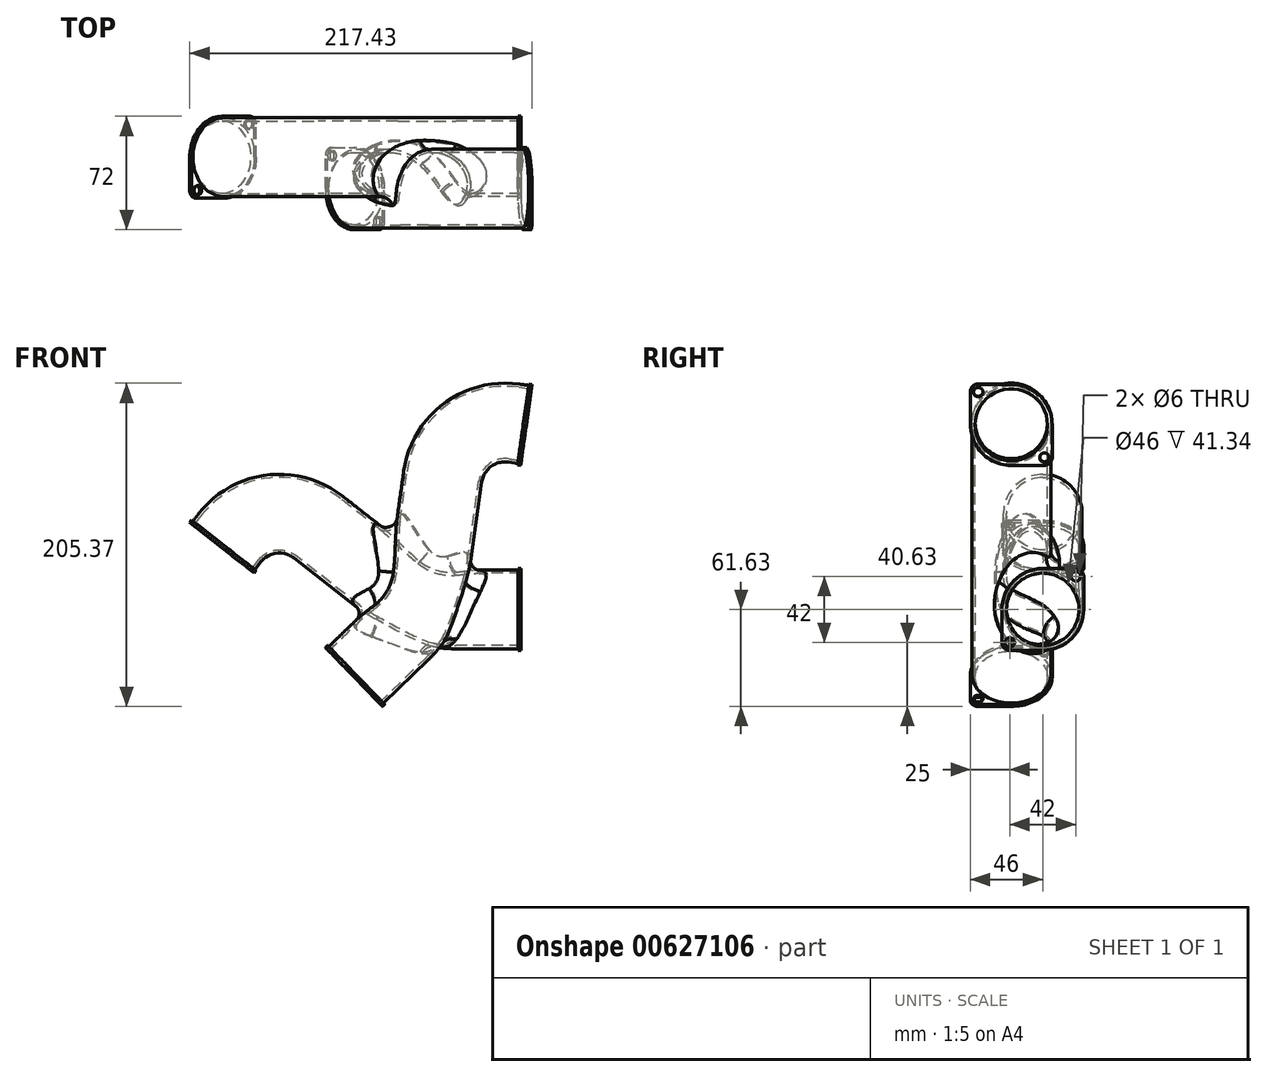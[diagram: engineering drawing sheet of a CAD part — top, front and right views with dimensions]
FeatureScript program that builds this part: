
annotation { "Feature Type Name" : "Feature", "Feature Type Description" : "" }
export const myFeature = defineFeature(function(context is Context, id is Id, definition is map)
    precondition{}
    {
        {
            var Q0;
            Q0=qCreatedBy(makeId("Right.planeOp"),FACE);
            var sketch = newSketch(context, id + "F0", { "sketchPlane" : qUnion([Q0])});
            skLineSegment(sketch, "E0.bottom", {"start": v(0, 26) * mm, "end": v(21, 26) * mm});
            skLineSegment(sketch, "E0.top", {"start": v(-21, -26) * mm, "end": v(0, -26) * mm});
            skLineSegment(sketch, "E0.left", {"start": v(-26, 0) * mm, "end": v(-26, -21) * mm});
            skLineSegment(sketch, "E0.right", {"start": v(26, 21) * mm, "end": v(26, 0) * mm});
            skPoint(sketch, "E0.middle", {"position": v(0, 0) * mm});
            skPoint(sketch, "E1.visualSharp", {"position": v(-26, 26) * mm});
            skArc(sketch, "E1.filletArc", {"start": v(0, 26) * mm, "mid": v(-18.38, 18.38) * mm, "end": v(-26, 0) * mm});
            skPoint(sketch, "E2.visualSharp", {"position": v(26, -26) * mm});
            skArc(sketch, "E2.filletArc", {"start": v(0, -26) * mm, "mid": v(18.38, -18.38) * mm, "end": v(26, 0) * mm});
            skPoint(sketch, "E3.visualSharp", {"position": v(-26, -26) * mm});
            skArc(sketch, "E3.filletArc", {"start": v(-26, -21) * mm, "mid": v(-24.54, -24.54) * mm, "end": v(-21, -26) * mm});
            skPoint(sketch, "E4.visualSharp", {"position": v(26, 26) * mm});
            skArc(sketch, "E4.filletArc", {"start": v(26, 21) * mm, "mid": v(24.54, 24.54) * mm, "end": v(21, 26) * mm});
            skCircle(sketch, "E5", {"center": v(21, 21) * mm, "radius": 3 * mm});
            skCircle(sketch, "E6", {"center": v(-21, -21) * mm, "radius": 3 * mm});
            skSolve(sketch);
        }
        {
            var Q0;
            Q0 = qSketchRegion(id + "F0", true);
            extrude(context, id + "F1", {"entities" : qUnion([Q0]), "depth" : 2 * mm, "offsetDistance" : 25 * mm});
        }
        {
            var Q0;
            Q0=makeQuery(id+"F1.opExtrude","CAP_FACE",FACE,{"disambiguationData":[OSD([sQuery(id+"F0.wireOp",EDGE,"E0.bottom"),sQuery(id+"F0.wireOp",EDGE,"E0.top"),sQuery(id+"F0.wireOp",EDGE,"E0.left"),sQuery(id+"F0.wireOp",EDGE,"E0.right"),sQuery(id+"F0.wireOp",EDGE,"E1.filletArc"),sQuery(id+"F0.wireOp",EDGE,"E2.filletArc"),sQuery(id+"F0.wireOp",EDGE,"E3.filletArc"),sQuery(id+"F0.wireOp",EDGE,"E4.filletArc"),sQuery(id+"F0.wireOp",EDGE,"E5"),sQuery(id+"F0.wireOp",EDGE,"E6")])],"isStart":true});
            var sketch = newSketch(context, id + "F2", { "sketchPlane" : qUnion([Q0])});
            skCircle(sketch, "E7", {"center": v(0, 0) * mm, "radius": 25 * mm});
            skSolve(sketch);
        }
        {
            var Q0;
            Q0=qCreatedBy(makeId("Front.planeOp"),FACE);
            var sketch = newSketch(context, id + "F3", { "sketchPlane" : qUnion([Q0])});
            skLineSegment(sketch, "E8", {"start": v(0, 0) * mm, "end": v(-39.34, 0) * mm});
            skLineSegment(sketch, "E9", {"start": v(-76.28, 12.72) * mm, "end": v(-126.98, 52.33) * mm});
            skLineSegment(sketch, "E10", {"start": v(-183.13, 45.44) * mm, "end": v(-186.82, 40.7) * mm});
            skPoint(sketch, "E11.visualSharp", {"position": v(-60, 0) * mm});
            skArc(sketch, "E11.filletArc", {"start": v(-76.28, 12.72) * mm, "mid": v(-58.87, 3.27) * mm, "end": v(-39.34, 0) * mm});
            skPoint(sketch, "E12.visualSharp", {"position": v(-158.5, 76.96) * mm});
            skArc(sketch, "E12.filletArc", {"start": v(-126.98, 52.33) * mm, "mid": v(-156.48, 60.51) * mm, "end": v(-183.13, 45.44) * mm});
            skSolve(sketch);
        }
        {
            var Q0;
            Q0=makeQuery(id+"F2.imprint","IMPRINT",FACE,{"disambiguationData":[TD([[makeQuery(id+"F2.imprint","IMPRINT",EDGE,{"derivedFrom":sQuery(id+"F2.wireOp",EDGE,"E7")}),1.0]])]});
            var Q1;
            Q1=sQuery(id+"F3.wireOp",EDGE,"E8");
            var Q2;
            Q2=sQuery(id+"F3.wireOp",EDGE,"E11.filletArc");
            var Q3;
            Q3=sQuery(id+"F3.wireOp",EDGE,"E9");
            var Q4;
            Q4=sQuery(id+"F3.wireOp",EDGE,"E12.filletArc");
            var Q5;
            Q5=sQuery(id+"F3.wireOp",EDGE,"E10");
            sweep(context, id + "F4", {"operationType" : NewBodyOperationType.ADD, "profiles" : qUnion([Q0]), "path" : qUnion([Q1, Q2, Q3, Q4, Q5])});
        }
        {
            var Q0;
            Q0=makeQuery(id+"F4.opSweep","CAP_FACE",FACE,{"disambiguationData":[OSD([sQuery(id+"F2.wireOp",EDGE,"E7"),sQuery(id+"F3.wireOp",VERTEX,"E10.end")])],"isStart":false});
            var sketch = newSketch(context, id + "F5", { "sketchPlane" : qUnion([Q0])});
            skLineSegment(sketch, "E13.bottom", {"start": v(-193.28, 26) * mm, "end": v(-172.28, 26) * mm});
            skLineSegment(sketch, "E13.top", {"start": v(-172.28, -26) * mm, "end": v(-151.28, -26) * mm});
            skLineSegment(sketch, "E13.left", {"start": v(-198.28, 21) * mm, "end": v(-198.28, 0) * mm});
            skLineSegment(sketch, "E13.right", {"start": v(-146.28, 0) * mm, "end": v(-146.28, -21) * mm});
            skPoint(sketch, "E13.middle", {"position": v(-172.28, 0) * mm});
            skPoint(sketch, "E14.visualSharp", {"position": v(-198.28, -26) * mm});
            skArc(sketch, "E14.filletArc", {"start": v(-198.28, 0) * mm, "mid": v(-190.67, -18.38) * mm, "end": v(-172.28, -26) * mm});
            skPoint(sketch, "E15.visualSharp", {"position": v(-146.28, 26) * mm});
            skArc(sketch, "E15.filletArc", {"start": v(-146.28, 0) * mm, "mid": v(-153.9, 18.38) * mm, "end": v(-172.28, 26) * mm});
            skPoint(sketch, "E16.visualSharp", {"position": v(-146.28, -26) * mm});
            skArc(sketch, "E16.filletArc", {"start": v(-151.28, -26) * mm, "mid": v(-147.75, -24.54) * mm, "end": v(-146.28, -21) * mm});
            skPoint(sketch, "E17.visualSharp", {"position": v(-198.28, 26) * mm});
            skArc(sketch, "E17.filletArc", {"start": v(-193.28, 26) * mm, "mid": v(-196.82, 24.54) * mm, "end": v(-198.28, 21) * mm});
            skCircle(sketch, "E18", {"center": v(-193.28, 21) * mm, "radius": 3 * mm});
            skCircle(sketch, "E19", {"center": v(-151.28, -21) * mm, "radius": 3 * mm});
            skSolve(sketch);
        }
        {
            var Q0;
            Q0 = qSketchRegion(id + "F5", true);
            extrude(context, id + "F6", {"entities" : qUnion([Q0]), "operationType" : NewBodyOperationType.ADD, "depth" : 2 * mm, "offsetDistance" : 25 * mm});
        }
        {
            var Q0;
            Q0=qCreatedBy(makeId("Top.planeOp"),FACE);
            var sketch = newSketch(context, id + "F7", { "sketchPlane" : qUnion([Q0])});
            skLineSegment(sketch, "E20", {"start": v(-59.8, 45.05) * mm, "end": v(-59.8, -43.57) * mm, "construction": true});
            skSolve(sketch);
        }
        {
            var Q0;
            Q0=sQuery(id+"F7.wireOp",EDGE,"E20");
            var Q1;
            Q1=makeQuery(id+"F1.opExtrude","CAP_FACE",FACE,{"disambiguationData":[OSD([sQuery(id+"F0.wireOp",EDGE,"E0.bottom"),sQuery(id+"F0.wireOp",EDGE,"E0.top"),sQuery(id+"F0.wireOp",EDGE,"E0.left"),sQuery(id+"F0.wireOp",EDGE,"E0.right"),sQuery(id+"F0.wireOp",EDGE,"E1.filletArc"),sQuery(id+"F0.wireOp",EDGE,"E2.filletArc"),sQuery(id+"F0.wireOp",EDGE,"E3.filletArc"),sQuery(id+"F0.wireOp",EDGE,"E4.filletArc"),sQuery(id+"F0.wireOp",EDGE,"E5"),sQuery(id+"F0.wireOp",EDGE,"E6")])],"isStart":false});
            cPlane(context, id + "F8", {"entities" : qUnion([Q0, Q1]), "cplaneType" : CPlaneType.LINE_ANGLE, "offset" : 25 * mm, "angle" : 22 * degree, "width" : 150 * mm, "height" : 150 * mm});
        }
        {
            var Q0;
            Q0=makeQuery(id+"F1.opExtrude","SWEPT_BODY",BODY,{"disambiguationData":[OSD([sQuery(id+"F0.wireOp",EDGE,"E0.bottom"),sQuery(id+"F0.wireOp",EDGE,"E0.top"),sQuery(id+"F0.wireOp",EDGE,"E0.left"),sQuery(id+"F0.wireOp",EDGE,"E0.right"),sQuery(id+"F0.wireOp",EDGE,"E1.filletArc"),sQuery(id+"F0.wireOp",EDGE,"E2.filletArc"),sQuery(id+"F0.wireOp",EDGE,"E3.filletArc"),sQuery(id+"F0.wireOp",EDGE,"E4.filletArc"),sQuery(id+"F0.wireOp",EDGE,"E5"),sQuery(id+"F0.wireOp",EDGE,"E6")])]});
            var Q1;
            Q1=qCreatedBy(id+"F8.planeOp",FACE);
            mirror(context, id + "F9", {"entities" : qUnion([Q0]), "mirrorPlane" : qUnion([Q1])});
        }
        {
            var Q0;
            Q0=makeQuery(id+"F1.opExtrude","SWEPT_BODY",BODY,{"disambiguationData":[OSD([sQuery(id+"F0.wireOp",EDGE,"E0.bottom"),sQuery(id+"F0.wireOp",EDGE,"E0.top"),sQuery(id+"F0.wireOp",EDGE,"E0.left"),sQuery(id+"F0.wireOp",EDGE,"E0.right"),sQuery(id+"F0.wireOp",EDGE,"E1.filletArc"),sQuery(id+"F0.wireOp",EDGE,"E2.filletArc"),sQuery(id+"F0.wireOp",EDGE,"E3.filletArc"),sQuery(id+"F0.wireOp",EDGE,"E4.filletArc"),sQuery(id+"F0.wireOp",EDGE,"E5"),sQuery(id+"F0.wireOp",EDGE,"E6")])]});
            transform(context, id + "F10", {"entities" : qUnion([Q0]), "transformType" : TransformType.TRANSLATION_3D, "dx" : 0 * mm, "dy" : 20 * mm, "dz" : 0 * mm, "makeCopy" : false});
        }
        {
            var Q0;
            Q0=makeQuery(id+"F1.opExtrude","SWEPT_BODY",BODY,{"disambiguationData":[OSD([sQuery(id+"F0.wireOp",EDGE,"E0.bottom"),sQuery(id+"F0.wireOp",EDGE,"E0.top"),sQuery(id+"F0.wireOp",EDGE,"E0.left"),sQuery(id+"F0.wireOp",EDGE,"E0.right"),sQuery(id+"F0.wireOp",EDGE,"E1.filletArc"),sQuery(id+"F0.wireOp",EDGE,"E2.filletArc"),sQuery(id+"F0.wireOp",EDGE,"E3.filletArc"),sQuery(id+"F0.wireOp",EDGE,"E4.filletArc"),sQuery(id+"F0.wireOp",EDGE,"E5"),sQuery(id+"F0.wireOp",EDGE,"E6")])]});
            var Q1;
            Q1=makeQuery(id+"F9.opPattern","COPY",BODY,{"derivedFrom":makeQuery(id+"F1.opExtrude","SWEPT_BODY",BODY,{"disambiguationData":[OSD([sQuery(id+"F0.wireOp",EDGE,"E0.bottom"),sQuery(id+"F0.wireOp",EDGE,"E0.top"),sQuery(id+"F0.wireOp",EDGE,"E0.left"),sQuery(id+"F0.wireOp",EDGE,"E0.right"),sQuery(id+"F0.wireOp",EDGE,"E1.filletArc"),sQuery(id+"F0.wireOp",EDGE,"E2.filletArc"),sQuery(id+"F0.wireOp",EDGE,"E3.filletArc"),sQuery(id+"F0.wireOp",EDGE,"E4.filletArc"),sQuery(id+"F0.wireOp",EDGE,"E5"),sQuery(id+"F0.wireOp",EDGE,"E6")])]}),"instanceName":"1"});
            booleanBodies(context, id + "F11", {"operationType" : BooleanOperationType.UNION, "tools" : qUnion([Q0, Q1])});
        }
        {
            var Q0;
            {var subQ0=sQuery(id+"F2.wireOp",EDGE,"E7");Q0=makeQuery(id+"F11.opBoolean","INTERSECT",EDGE,{"derivedFrom":[makeQuery(id+"F4.opSweep","SWEPT_FACE",FACE,{"disambiguationData":[OSD([subQ0,sQuery(id+"F3.wireOp",EDGE,"E11.filletArc")])]}),makeQuery(id+"F9.opPattern","COPY",FACE,{"derivedFrom":makeQuery(id+"F4.opSweep","SWEPT_FACE",FACE,{"disambiguationData":[OSD([subQ0,sQuery(id+"F3.wireOp",EDGE,"E9")])]}),"instanceName":"1"})]});}
            fillet(context, id + "F12", {"entities" : qUnion([Q0]), "radius" : 10 * mm, "tangentPropagation" : true, "allowEdgeOverflow" : false});
        }
        {
            var Q0;
            Q0=makeQuery(id+"F6.opExtrude","CAP_FACE",FACE,{"disambiguationData":[OSD([sQuery(id+"F5.wireOp",EDGE,"E13.bottom"),sQuery(id+"F5.wireOp",EDGE,"E13.top"),sQuery(id+"F5.wireOp",EDGE,"E13.left"),sQuery(id+"F5.wireOp",EDGE,"E13.right"),sQuery(id+"F5.wireOp",EDGE,"E14.filletArc"),sQuery(id+"F5.wireOp",EDGE,"E15.filletArc"),sQuery(id+"F5.wireOp",EDGE,"E16.filletArc"),sQuery(id+"F5.wireOp",EDGE,"E17.filletArc"),sQuery(id+"F5.wireOp",EDGE,"E18"),sQuery(id+"F5.wireOp",EDGE,"E19")])],"isStart":false});
            var Q1;
            Q1=makeQuery(id+"F9.opPattern","COPY",FACE,{"derivedFrom":makeQuery(id+"F1.opExtrude","CAP_FACE",FACE,{"disambiguationData":[OSD([sQuery(id+"F0.wireOp",EDGE,"E0.bottom"),sQuery(id+"F0.wireOp",EDGE,"E0.top"),sQuery(id+"F0.wireOp",EDGE,"E0.left"),sQuery(id+"F0.wireOp",EDGE,"E0.right"),sQuery(id+"F0.wireOp",EDGE,"E1.filletArc"),sQuery(id+"F0.wireOp",EDGE,"E2.filletArc"),sQuery(id+"F0.wireOp",EDGE,"E3.filletArc"),sQuery(id+"F0.wireOp",EDGE,"E4.filletArc"),sQuery(id+"F0.wireOp",EDGE,"E5"),sQuery(id+"F0.wireOp",EDGE,"E6")])],"isStart":false}),"instanceName":"1"});
            var Q2;
            Q2=makeQuery(id+"F9.opPattern","COPY",FACE,{"derivedFrom":makeQuery(id+"F6.opExtrude","CAP_FACE",FACE,{"disambiguationData":[OSD([sQuery(id+"F5.wireOp",EDGE,"E13.bottom"),sQuery(id+"F5.wireOp",EDGE,"E13.top"),sQuery(id+"F5.wireOp",EDGE,"E13.left"),sQuery(id+"F5.wireOp",EDGE,"E13.right"),sQuery(id+"F5.wireOp",EDGE,"E14.filletArc"),sQuery(id+"F5.wireOp",EDGE,"E15.filletArc"),sQuery(id+"F5.wireOp",EDGE,"E16.filletArc"),sQuery(id+"F5.wireOp",EDGE,"E17.filletArc"),sQuery(id+"F5.wireOp",EDGE,"E18"),sQuery(id+"F5.wireOp",EDGE,"E19")])],"isStart":false}),"instanceName":"1"});
            var Q3;
            Q3=makeQuery(id+"F1.opExtrude","CAP_FACE",FACE,{"disambiguationData":[OSD([sQuery(id+"F0.wireOp",EDGE,"E0.bottom"),sQuery(id+"F0.wireOp",EDGE,"E0.top"),sQuery(id+"F0.wireOp",EDGE,"E0.left"),sQuery(id+"F0.wireOp",EDGE,"E0.right"),sQuery(id+"F0.wireOp",EDGE,"E1.filletArc"),sQuery(id+"F0.wireOp",EDGE,"E2.filletArc"),sQuery(id+"F0.wireOp",EDGE,"E3.filletArc"),sQuery(id+"F0.wireOp",EDGE,"E4.filletArc"),sQuery(id+"F0.wireOp",EDGE,"E5"),sQuery(id+"F0.wireOp",EDGE,"E6")])],"isStart":false});
            shell(context, id + "F13", {"entities" : qUnion([Q0, Q1, Q2, Q3]), "thickness" : 2 * mm});
        }
    });
